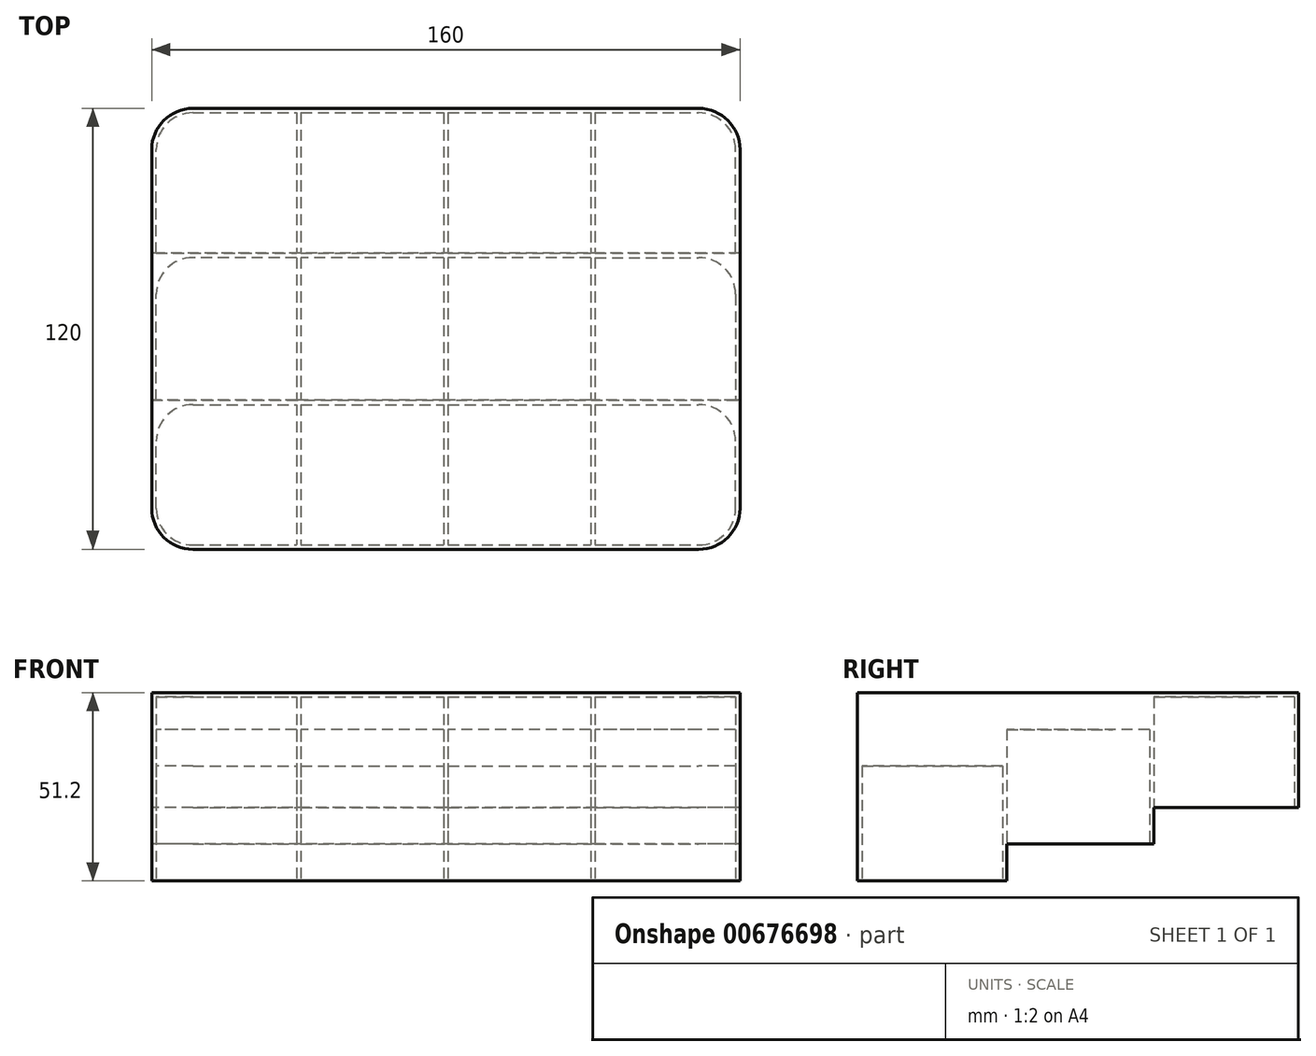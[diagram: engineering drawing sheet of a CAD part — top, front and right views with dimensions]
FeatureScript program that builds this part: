
annotation { "Feature Type Name" : "Feature", "Feature Type Description" : "" }
export const myFeature = defineFeature(function(context is Context, id is Id, definition is map)
    precondition{}
    {
        {
            var Q0;
            Q0=qCreatedBy(makeId("Top.planeOp"),FACE);
            var sketch = newSketch(context, id + "F0", { "sketchPlane" : qUnion([Q0])});
            skLineSegment(sketch, "E0.bottom", {"start": v(-160, -120) * mm, "end": v(0, -120) * mm});
            skLineSegment(sketch, "E0.top", {"start": v(-160, 0) * mm, "end": v(0, 0) * mm});
            skLineSegment(sketch, "E0.left", {"start": v(-160, -120) * mm, "end": v(-160, 0) * mm});
            skLineSegment(sketch, "E0.right", {"start": v(0, -120) * mm, "end": v(0, 0) * mm});
            skLineSegment(sketch, "E1.0", {"start": v(-158.8, -1.2) * mm, "end": v(-120.6, -1.2) * mm});
            skLineSegment(sketch, "E2.0", {"start": v(-158.8, -118.8) * mm, "end": v(-158.8, -80.6) * mm});
            skLineSegment(sketch, "E3.0", {"start": v(-158.8, -118.8) * mm, "end": v(-120.6, -118.8) * mm});
            skLineSegment(sketch, "E4.0", {"start": v(-1.2, -118.8) * mm, "end": v(-1.2, -80.6) * mm});
            skLineSegment(sketch, "E5.0", {"start": v(-158.8, -40.6) * mm, "end": v(-120.6, -40.6) * mm});
            skLineSegment(sketch, "E6.0", {"start": v(-158.8, -80.6) * mm, "end": v(-120.6, -80.6) * mm});
            skLineSegment(sketch, "E7.0", {"start": v(-158.8, -79.4) * mm, "end": v(-120.6, -79.4) * mm});
            skLineSegment(sketch, "E8.0", {"start": v(-158.8, -39.4) * mm, "end": v(-120.6, -39.4) * mm});
            skLineSegment(sketch, "E9.0", {"start": v(-120.6, -1.2) * mm, "end": v(-120.6, -39.4) * mm});
            skLineSegment(sketch, "E10.0", {"start": v(-119.4, -1.2) * mm, "end": v(-119.4, -39.4) * mm});
            skLineSegment(sketch, "E11.0", {"start": v(-80.6, -1.2) * mm, "end": v(-80.6, -39.4) * mm});
            skLineSegment(sketch, "E12.0", {"start": v(-79.4, -1.2) * mm, "end": v(-79.4, -39.4) * mm});
            skLineSegment(sketch, "E13.0", {"start": v(-40.6, -1.2) * mm, "end": v(-40.6, -39.4) * mm});
            skLineSegment(sketch, "E14.0", {"start": v(-39.4, -1.2) * mm, "end": v(-39.4, -39.4) * mm});
            skPoint(sketch, "E15.orphan", {"position": v(-160, -40) * mm});
            skLineSegment(sketch, "E16.trimOffspring", {"start": v(-158.8, -79.4) * mm, "end": v(-158.8, -40.6) * mm});
            skPoint(sketch, "E17.orphan", {"position": v(-160, -80) * mm});
            skPoint(sketch, "E18.orphan", {"position": v(-120, -120) * mm});
            skPoint(sketch, "E19.orphan", {"position": v(-80, -120) * mm});
            skPoint(sketch, "E20.orphan", {"position": v(0, -40) * mm});
            skLineSegment(sketch, "E21.trimOffspring", {"start": v(-119.4, -39.4) * mm, "end": v(-80.6, -39.4) * mm});
            skLineSegment(sketch, "E22.trimOffspring", {"start": v(-119.4, -40.6) * mm, "end": v(-80.6, -40.6) * mm});
            skLineSegment(sketch, "E23.trimOffspring", {"start": v(-120.6, -40.6) * mm, "end": v(-120.6, -79.4) * mm});
            skLineSegment(sketch, "E24.trimOffspring", {"start": v(-119.4, -40.6) * mm, "end": v(-119.4, -79.4) * mm});
            skLineSegment(sketch, "E25.trimOffspring", {"start": v(-119.4, -79.4) * mm, "end": v(-80.6, -79.4) * mm});
            skLineSegment(sketch, "E26.trimOffspring", {"start": v(-120.6, -80.6) * mm, "end": v(-120.6, -118.8) * mm});
            skLineSegment(sketch, "E27.trimOffspring", {"start": v(-119.4, -80.6) * mm, "end": v(-119.4, -118.8) * mm});
            skLineSegment(sketch, "E28.trimOffspring", {"start": v(-119.4, -80.6) * mm, "end": v(-80.6, -80.6) * mm});
            skLineSegment(sketch, "E29.trimOffspring", {"start": v(-80.6, -40.6) * mm, "end": v(-80.6, -79.4) * mm});
            skLineSegment(sketch, "E30.trimOffspring", {"start": v(-79.4, -39.4) * mm, "end": v(-40.6, -39.4) * mm});
            skLineSegment(sketch, "E31.trimOffspring", {"start": v(-79.4, -40.6) * mm, "end": v(-79.4, -79.4) * mm});
            skLineSegment(sketch, "E32.trimOffspring", {"start": v(-79.4, -40.6) * mm, "end": v(-40.6, -40.6) * mm});
            skLineSegment(sketch, "E33.trimOffspring", {"start": v(-40.6, -40.6) * mm, "end": v(-40.6, -79.4) * mm});
            skLineSegment(sketch, "E34.trimOffspring", {"start": v(-39.4, -39.4) * mm, "end": v(-1.2, -39.4) * mm});
            skLineSegment(sketch, "E35.trimOffspring", {"start": v(-39.4, -40.6) * mm, "end": v(-1.2, -40.6) * mm});
            skLineSegment(sketch, "E36.trimOffspring", {"start": v(-39.4, -40.6) * mm, "end": v(-39.4, -79.4) * mm});
            skLineSegment(sketch, "E37.trimOffspring", {"start": v(-39.4, -79.4) * mm, "end": v(-1.2, -79.4) * mm});
            skLineSegment(sketch, "E38.trimOffspring", {"start": v(-39.4, -80.6) * mm, "end": v(-1.2, -80.6) * mm});
            skLineSegment(sketch, "E39.trimOffspring", {"start": v(-39.4, -80.6) * mm, "end": v(-39.4, -118.8) * mm});
            skLineSegment(sketch, "E40.trimOffspring", {"start": v(-40.6, -80.6) * mm, "end": v(-40.6, -118.8) * mm});
            skLineSegment(sketch, "E41.trimOffspring", {"start": v(-79.4, -79.4) * mm, "end": v(-40.6, -79.4) * mm});
            skLineSegment(sketch, "E42.trimOffspring", {"start": v(-79.4, -80.6) * mm, "end": v(-40.6, -80.6) * mm});
            skLineSegment(sketch, "E43.trimOffspring", {"start": v(-80.6, -80.6) * mm, "end": v(-80.6, -118.8) * mm});
            skLineSegment(sketch, "E44.trimOffspring", {"start": v(-79.4, -80.6) * mm, "end": v(-79.4, -118.8) * mm});
            skLineSegment(sketch, "E45.trimOffspring", {"start": v(-1.2, -79.4) * mm, "end": v(-1.2, -40.6) * mm});
            skLineSegment(sketch, "E46.trimOffspring", {"start": v(-1.2, -39.4) * mm, "end": v(-1.2, -1.2) * mm});
            skLineSegment(sketch, "E47.trimOffspring", {"start": v(-39.4, -1.2) * mm, "end": v(-1.2, -1.2) * mm});
            skLineSegment(sketch, "E48.trimOffspring", {"start": v(-79.4, -1.2) * mm, "end": v(-40.6, -1.2) * mm});
            skLineSegment(sketch, "E49.trimOffspring", {"start": v(-119.4, -1.2) * mm, "end": v(-80.6, -1.2) * mm});
            skLineSegment(sketch, "E50.trimOffspring", {"start": v(-158.8, -39.4) * mm, "end": v(-158.8, -1.2) * mm});
            skLineSegment(sketch, "E51.trimOffspring", {"start": v(-119.4, -118.8) * mm, "end": v(-80.6, -118.8) * mm});
            skLineSegment(sketch, "E52.trimOffspring", {"start": v(-79.4, -118.8) * mm, "end": v(-40.6, -118.8) * mm});
            skLineSegment(sketch, "E53.trimOffspring", {"start": v(-39.4, -118.8) * mm, "end": v(-1.2, -118.8) * mm});
            skSolve(sketch);
        }
        {
            var Q0;
            Q0=makeQuery(id+"F0.imprint","IMPRINT",FACE,{"disambiguationData":[TD([[makeQuery(id+"F0.imprint","IMPRINT",EDGE,{"derivedFrom":sQuery(id+"F0.wireOp",EDGE,"E0.bottom")}),1.0]])]});
            extrude(context, id + "F1", {"entities" : qUnion([Q0]), "depth" : 50 * mm});
        }
        {
            var Q0;
            Q0=makeQuery(id+"F1.opExtrude","CAP_FACE",FACE,{"disambiguationData":[OSD([sQuery(id+"F0.wireOp",EDGE,"E0.bottom"),sQuery(id+"F0.wireOp",EDGE,"E0.top"),sQuery(id+"F0.wireOp",EDGE,"E0.left"),sQuery(id+"F0.wireOp",EDGE,"E0.right"),sQuery(id+"F0.wireOp",EDGE,"E1.0"),sQuery(id+"F0.wireOp",EDGE,"E2.0"),sQuery(id+"F0.wireOp",EDGE,"E3.0"),sQuery(id+"F0.wireOp",EDGE,"E4.0"),sQuery(id+"F0.wireOp",EDGE,"E5.0"),sQuery(id+"F0.wireOp",EDGE,"E6.0"),sQuery(id+"F0.wireOp",EDGE,"E7.0"),sQuery(id+"F0.wireOp",EDGE,"E8.0"),sQuery(id+"F0.wireOp",EDGE,"E9.0"),sQuery(id+"F0.wireOp",EDGE,"E10.0"),sQuery(id+"F0.wireOp",EDGE,"E11.0"),sQuery(id+"F0.wireOp",EDGE,"E12.0"),sQuery(id+"F0.wireOp",EDGE,"E13.0"),sQuery(id+"F0.wireOp",EDGE,"E14.0"),sQuery(id+"F0.wireOp",EDGE,"E16.trimOffspring"),sQuery(id+"F0.wireOp",EDGE,"E21.trimOffspring"),sQuery(id+"F0.wireOp",EDGE,"E22.trimOffspring"),sQuery(id+"F0.wireOp",EDGE,"E23.trimOffspring"),sQuery(id+"F0.wireOp",EDGE,"E24.trimOffspring"),sQuery(id+"F0.wireOp",EDGE,"E25.trimOffspring"),sQuery(id+"F0.wireOp",EDGE,"E26.trimOffspring"),sQuery(id+"F0.wireOp",EDGE,"E27.trimOffspring"),sQuery(id+"F0.wireOp",EDGE,"E28.trimOffspring"),sQuery(id+"F0.wireOp",EDGE,"E29.trimOffspring"),sQuery(id+"F0.wireOp",EDGE,"E30.trimOffspring"),sQuery(id+"F0.wireOp",EDGE,"E31.trimOffspring"),sQuery(id+"F0.wireOp",EDGE,"E32.trimOffspring"),sQuery(id+"F0.wireOp",EDGE,"E33.trimOffspring"),sQuery(id+"F0.wireOp",EDGE,"E34.trimOffspring"),sQuery(id+"F0.wireOp",EDGE,"E35.trimOffspring"),sQuery(id+"F0.wireOp",EDGE,"E36.trimOffspring"),sQuery(id+"F0.wireOp",EDGE,"E37.trimOffspring"),sQuery(id+"F0.wireOp",EDGE,"E38.trimOffspring"),sQuery(id+"F0.wireOp",EDGE,"E39.trimOffspring"),sQuery(id+"F0.wireOp",EDGE,"E40.trimOffspring"),sQuery(id+"F0.wireOp",EDGE,"E41.trimOffspring"),sQuery(id+"F0.wireOp",EDGE,"E42.trimOffspring"),sQuery(id+"F0.wireOp",EDGE,"E43.trimOffspring"),sQuery(id+"F0.wireOp",EDGE,"E44.trimOffspring"),sQuery(id+"F0.wireOp",EDGE,"E45.trimOffspring"),sQuery(id+"F0.wireOp",EDGE,"E46.trimOffspring"),sQuery(id+"F0.wireOp",EDGE,"E47.trimOffspring"),sQuery(id+"F0.wireOp",EDGE,"E48.trimOffspring"),sQuery(id+"F0.wireOp",EDGE,"E49.trimOffspring"),sQuery(id+"F0.wireOp",EDGE,"E50.trimOffspring"),sQuery(id+"F0.wireOp",EDGE,"E51.trimOffspring"),sQuery(id+"F0.wireOp",EDGE,"E52.trimOffspring"),sQuery(id+"F0.wireOp",EDGE,"E53.trimOffspring")])],"isStart":false});
            var sketch = newSketch(context, id + "F2", { "sketchPlane" : qUnion([Q0])});
            skLineSegment(sketch, "E54.bottom", {"start": v(-160, 0) * mm, "end": v(0, 0) * mm});
            skLineSegment(sketch, "E54.top", {"start": v(-160, -120) * mm, "end": v(0, -120) * mm});
            skLineSegment(sketch, "E54.left", {"start": v(-160, 0) * mm, "end": v(-160, -120) * mm});
            skLineSegment(sketch, "E54.right", {"start": v(0, 0) * mm, "end": v(0, -120) * mm});
            skSolve(sketch);
        }
        {
            var Q0;
            Q0=qSketchRegion(id+"F2",true);
            extrude(context, id + "F3", {"entities" : qUnion([Q0]), "operationType" : NewBodyOperationType.ADD, "depth" : 1.2 * mm});
        }
        {
            var Q0;
            Q0=makeQuery(id+"F3.boolean.opBoolean","MERGE",FACE,{"derivedFrom":[makeQuery(id+"F1.opExtrude","SWEPT_FACE",FACE,{"disambiguationData":[OSD([sQuery(id+"F0.wireOp",EDGE,"E0.left")])]}),makeQuery(id+"F3.opExtrude","SWEPT_FACE",FACE,{"disambiguationData":[OSD([sQuery(id+"F2.wireOp",EDGE,"E54.left")])]})]});
            var sketch = newSketch(context, id + "F4", { "sketchPlane" : qUnion([Q0])});
            skLineSegment(sketch, "E55.0.0", {"start": v(79.4, 0) * mm, "end": v(40.6, 0) * mm, "construction": true});
            skLineSegment(sketch, "E55.0.1", {"start": v(40.6, 10) * mm, "end": v(40.6, 50) * mm, "construction": true});
            skLineSegment(sketch, "E55.0.2", {"start": v(40.6, 50) * mm, "end": v(79.4, 50) * mm, "construction": true});
            skLineSegment(sketch, "E55.0.3", {"start": v(79.4, 50) * mm, "end": v(79.4, 0) * mm, "construction": true});
            skLineSegment(sketch, "E56.0.0", {"start": v(39.4, 0) * mm, "end": v(1.2, 0) * mm, "construction": true});
            skLineSegment(sketch, "E56.0.1", {"start": v(1.2, 20) * mm, "end": v(1.2, 50) * mm, "construction": true});
            skLineSegment(sketch, "E56.0.2", {"start": v(1.2, 50) * mm, "end": v(39.4, 50) * mm, "construction": true});
            skLineSegment(sketch, "E56.0.3", {"start": v(39.4, 50) * mm, "end": v(39.4, 10) * mm, "construction": true});
            skLineSegment(sketch, "E57", {"start": v(79.4, 0) * mm, "end": v(79.4, 10) * mm, "construction": true});
            skLineSegment(sketch, "E58", {"start": v(79.4, 10) * mm, "end": v(39.4, 10) * mm, "construction": true});
            skLineSegment(sketch, "E59", {"start": v(39.4, 10) * mm, "end": v(39.4, 20) * mm, "construction": true});
            skLineSegment(sketch, "E60", {"start": v(39.4, 20) * mm, "end": v(0, 20) * mm, "construction": true});
            skLineSegment(sketch, "E61", {"start": v(79.4, 10) * mm, "end": v(39.4, 10) * mm});
            skLineSegment(sketch, "E62", {"start": v(39.4, 20) * mm, "end": v(39.4, 10) * mm});
            skLineSegment(sketch, "E63", {"start": v(39.4, 20) * mm, "end": v(0, 20) * mm});
            skLineSegment(sketch, "E64", {"start": v(0, 20) * mm, "end": v(0, 0) * mm});
            skLineSegment(sketch, "E65", {"start": v(0, 0) * mm, "end": v(79.4, 0) * mm});
            skLineSegment(sketch, "E66", {"start": v(79.4, 10) * mm, "end": v(79.4, 0) * mm});
            skSolve(sketch);
        }
        {
            var Q0;
            Q0=makeQuery(id+"F4.imprint","IMPRINT",FACE,{"disambiguationData":[TD([[makeQuery(id+"F4.imprint","IMPRINT",EDGE,{"derivedFrom":sQuery(id+"F4.wireOp",EDGE,"E61")}),1.0]])]});
            extrude(context, id + "F5", {"entities" : qUnion([Q0]), "operationType" : NewBodyOperationType.REMOVE, "endBound" : BoundingType.THROUGH_ALL, "oppositeDirection" : true, "depth" : 25 * mm});
        }
        {
            var Q0;
            Q0=makeQuery(id+"F3.boolean.opBoolean","MERGE",FACE,{"derivedFrom":[makeQuery(id+"F1.opExtrude","SWEPT_FACE",FACE,{"disambiguationData":[OSD([sQuery(id+"F0.wireOp",EDGE,"E0.left")])]}),makeQuery(id+"F3.opExtrude","SWEPT_FACE",FACE,{"disambiguationData":[OSD([sQuery(id+"F2.wireOp",EDGE,"E54.left")])]})]});
            var sketch = newSketch(context, id + "F6", { "sketchPlane" : qUnion([Q0])});
            skLineSegment(sketch, "E67.0.0", {"start": v(80.6, 0) * mm, "end": v(118.8, 0) * mm});
            skLineSegment(sketch, "E67.0.1", {"start": v(118.8, 31.2) * mm, "end": v(118.8, 50) * mm});
            skLineSegment(sketch, "E67.0.2", {"start": v(118.8, 50) * mm, "end": v(40.6, 50) * mm});
            skLineSegment(sketch, "E68.0.0", {"start": v(40.6, 50) * mm, "end": v(40.6, 10) * mm});
            skLineSegment(sketch, "E68.0.1", {"start": v(40.6, 10) * mm, "end": v(79.4, 10) * mm});
            skLineSegment(sketch, "E68.0.2", {"start": v(79.4, 31.2) * mm, "end": v(79.4, 41.2) * mm});
            skLineSegment(sketch, "E69", {"start": v(118.8, 31.2) * mm, "end": v(79.4, 31.2) * mm});
            skLineSegment(sketch, "E70", {"start": v(79.4, 41.2) * mm, "end": v(40.6, 41.2) * mm});
            skPoint(sketch, "E71.orphan", {"position": v(80.6, 50) * mm});
            skSolve(sketch);
        }
        {
            var Q0;
            Q0=makeQuery(id+"F6.imprint","IMPRINT",FACE,{"disambiguationData":[TD([[makeQuery(id+"F6.imprint","IMPRINT",EDGE,{"derivedFrom":sQuery(id+"F6.wireOp",EDGE,"E67.0.1")}),1.0]])]});
            var Q1;
            Q1=makeQuery(id+"F1.opExtrude","SWEPT_FACE",FACE,{"disambiguationData":[OSD([sQuery(id+"F0.wireOp",EDGE,"E45.trimOffspring")])]});
            extrude(context, id + "F7", {"entities" : qUnion([Q0]), "operationType" : NewBodyOperationType.ADD, "endBound" : BoundingType.UP_TO_SURFACE, "oppositeDirection" : true, "endBoundEntityFace" : qUnion([Q1]), "depth" : 25 * mm});
        }
        {
            var Q0;
            Q0=makeQuery(id+"F1.opExtrude","SWEPT_EDGE",EDGE,{"disambiguationData":[OSD([sQuery(id+"F0.wireOp",EDGE,"E4.0"),sQuery(id+"F0.wireOp",EDGE,"E53.trimOffspring")])]});
            var Q1;
            Q1=makeQuery(id+"F1.opExtrude","SWEPT_EDGE",EDGE,{"disambiguationData":[OSD([sQuery(id+"F0.wireOp",EDGE,"E46.trimOffspring"),sQuery(id+"F0.wireOp",EDGE,"E47.trimOffspring")])]});
            var Q2;
            Q2=makeQuery(id+"F1.opExtrude","SWEPT_EDGE",EDGE,{"disambiguationData":[OSD([sQuery(id+"F0.wireOp",EDGE,"E2.0"),sQuery(id+"F0.wireOp",EDGE,"E3.0")])]});
            var Q3;
            Q3=makeQuery(id+"F1.opExtrude","SWEPT_EDGE",EDGE,{"disambiguationData":[OSD([sQuery(id+"F0.wireOp",EDGE,"E1.0"),sQuery(id+"F0.wireOp",EDGE,"E50.trimOffspring")])]});
            fillet(context, id + "F8", {"entities" : qUnion([Q0, Q1, Q2, Q3]), "radius" : 10 * mm, "tangentPropagation" : true, "allowEdgeOverflow" : false});
        }
        {
            var Q0;
            Q0=makeQuery(id+"F3.boolean.opBoolean","MERGE",EDGE,{"derivedFrom":[makeQuery(id+"F1.opExtrude","SWEPT_EDGE",EDGE,{"disambiguationData":[OSD([sQuery(id+"F0.wireOp",EDGE,"E0.top"),sQuery(id+"F0.wireOp",EDGE,"E0.left")])]}),makeQuery(id+"F3.opExtrude","SWEPT_EDGE",EDGE,{"disambiguationData":[OSD([sQuery(id+"F2.wireOp",EDGE,"E54.bottom"),sQuery(id+"F2.wireOp",EDGE,"E54.left")])]})]});
            var Q1;
            Q1=makeQuery(id+"F3.boolean.opBoolean","MERGE",EDGE,{"derivedFrom":[makeQuery(id+"F1.opExtrude","SWEPT_EDGE",EDGE,{"disambiguationData":[OSD([sQuery(id+"F0.wireOp",EDGE,"E0.top"),sQuery(id+"F0.wireOp",EDGE,"E0.right")])]}),makeQuery(id+"F3.opExtrude","SWEPT_EDGE",EDGE,{"disambiguationData":[OSD([sQuery(id+"F2.wireOp",EDGE,"E54.bottom"),sQuery(id+"F2.wireOp",EDGE,"E54.right")])]})]});
            var Q2;
            Q2=makeQuery(id+"F3.boolean.opBoolean","MERGE",EDGE,{"derivedFrom":[makeQuery(id+"F1.opExtrude","SWEPT_EDGE",EDGE,{"disambiguationData":[OSD([sQuery(id+"F0.wireOp",EDGE,"E0.bottom"),sQuery(id+"F0.wireOp",EDGE,"E0.right")])]}),makeQuery(id+"F3.opExtrude","SWEPT_EDGE",EDGE,{"disambiguationData":[OSD([sQuery(id+"F2.wireOp",EDGE,"E54.top"),sQuery(id+"F2.wireOp",EDGE,"E54.right")])]})]});
            var Q3;
            Q3=makeQuery(id+"F3.boolean.opBoolean","MERGE",EDGE,{"derivedFrom":[makeQuery(id+"F1.opExtrude","SWEPT_EDGE",EDGE,{"disambiguationData":[OSD([sQuery(id+"F0.wireOp",EDGE,"E0.bottom"),sQuery(id+"F0.wireOp",EDGE,"E0.left")])]}),makeQuery(id+"F3.opExtrude","SWEPT_EDGE",EDGE,{"disambiguationData":[OSD([sQuery(id+"F2.wireOp",EDGE,"E54.top"),sQuery(id+"F2.wireOp",EDGE,"E54.left")])]})]});
            fillet(context, id + "F9", {"entities" : qUnion([Q0, Q1, Q2, Q3]), "radius" : 11.2 * mm, "tangentPropagation" : true, "allowEdgeOverflow" : false});
        }
        {
            var Q0;
            Q0=makeQuery(id+"F1.opExtrude","SWEPT_EDGE",EDGE,{"disambiguationData":[OSD([sQuery(id+"F0.wireOp",EDGE,"E2.0"),sQuery(id+"F0.wireOp",EDGE,"E6.0")])]});
            var Q1;
            Q1=makeQuery(id+"F1.opExtrude","SWEPT_EDGE",EDGE,{"disambiguationData":[OSD([sQuery(id+"F0.wireOp",EDGE,"E5.0"),sQuery(id+"F0.wireOp",EDGE,"E16.trimOffspring")])]});
            var Q2;
            Q2=makeQuery(id+"F1.opExtrude","SWEPT_EDGE",EDGE,{"disambiguationData":[OSD([sQuery(id+"F0.wireOp",EDGE,"E35.trimOffspring"),sQuery(id+"F0.wireOp",EDGE,"E45.trimOffspring")])]});
            var Q3;
            Q3=makeQuery(id+"F1.opExtrude","SWEPT_EDGE",EDGE,{"disambiguationData":[OSD([sQuery(id+"F0.wireOp",EDGE,"E4.0"),sQuery(id+"F0.wireOp",EDGE,"E38.trimOffspring")])]});
            fillet(context, id + "F10", {"entities" : qUnion([Q0, Q1, Q2, Q3]), "radius" : 10 * mm, "tangentPropagation" : true, "allowEdgeOverflow" : false});
        }
    });
